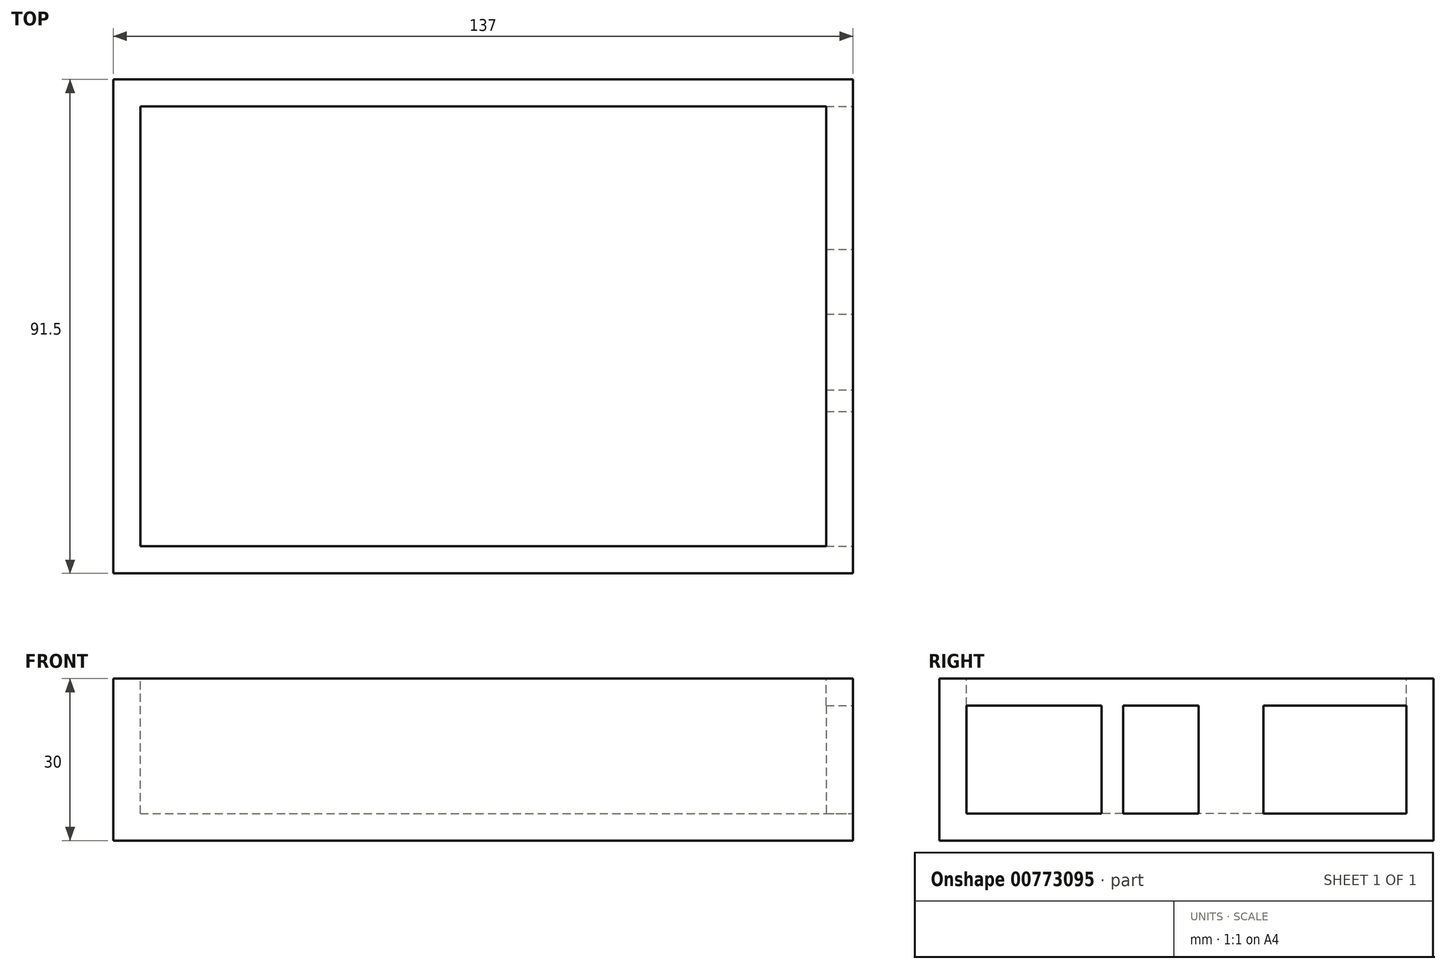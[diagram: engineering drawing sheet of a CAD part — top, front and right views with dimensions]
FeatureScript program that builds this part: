
annotation { "Feature Type Name" : "Feature", "Feature Type Description" : "" }
export const myFeature = defineFeature(function(context is Context, id is Id, definition is map)
    precondition{}
    {
        {
            var Q0;
            Q0=qCreatedBy(makeId("Top.planeOp"),FACE);
            var sketch = newSketch(context, id + "F0", { "sketchPlane" : qUnion([Q0])});
            skLineSegment(sketch, "E0.bottom", {"start": v(-74.24, 56.87) * mm, "end": v(62.76, 56.87) * mm});
            skLineSegment(sketch, "E0.top", {"start": v(-74.24, -34.63) * mm, "end": v(62.76, -34.63) * mm});
            skLineSegment(sketch, "E0.left", {"start": v(-74.24, 56.87) * mm, "end": v(-74.24, -34.63) * mm});
            skLineSegment(sketch, "E0.right", {"start": v(62.76, 56.87) * mm, "end": v(62.76, -34.63) * mm});
            skSolve(sketch);
        }
        {
            var Q0;
            Q0=makeQuery(id+"F0.imprint","IMPRINT",FACE,{"disambiguationData":[TD([[makeQuery(id+"F0.imprint","IMPRINT",EDGE,{"derivedFrom":sQuery(id+"F0.wireOp",EDGE,"E0.bottom")}),-1.0]])]});
            extrude(context, id + "F1", {"entities" : qUnion([Q0]), "depth" : 30 * mm, "offsetDistance" : 25 * mm});
        }
        {
            var Q0;
            Q0=makeQuery(id+"F1.opExtrude","CAP_FACE",FACE,{"disambiguationData":[OSD([sQuery(id+"F0.wireOp",EDGE,"E0.bottom"),sQuery(id+"F0.wireOp",EDGE,"E0.top"),sQuery(id+"F0.wireOp",EDGE,"E0.left"),sQuery(id+"F0.wireOp",EDGE,"E0.right")])],"isStart":false});
            var sketch = newSketch(context, id + "F2", { "sketchPlane" : qUnion([Q0])});
            skLineSegment(sketch, "E1", {"start": v(-74.24, 56.87) * mm, "end": v(-74.24, 51.87) * mm, "construction": true});
            skLineSegment(sketch, "E2", {"start": v(-74.24, 51.87) * mm, "end": v(-69.24, 51.87) * mm, "construction": true});
            skLineSegment(sketch, "E3", {"start": v(62.76, -34.63) * mm, "end": v(57.76, -34.63) * mm, "construction": true});
            skLineSegment(sketch, "E4", {"start": v(57.76, -34.63) * mm, "end": v(57.76, -29.63) * mm, "construction": true});
            skLineSegment(sketch, "E5.bottom", {"start": v(-69.24, 51.87) * mm, "end": v(57.76, 51.87) * mm});
            skLineSegment(sketch, "E5.top", {"start": v(-69.24, -29.63) * mm, "end": v(57.76, -29.63) * mm});
            skLineSegment(sketch, "E5.left", {"start": v(-69.24, 51.87) * mm, "end": v(-69.24, -29.63) * mm});
            skLineSegment(sketch, "E5.right", {"start": v(57.76, 51.87) * mm, "end": v(57.76, -29.63) * mm});
            skSolve(sketch);
        }
        {
            var Q0;
            Q0=makeQuery(id+"F2.imprint","IMPRINT",FACE,{"disambiguationData":[TD([[makeQuery(id+"F2.imprint","IMPRINT",EDGE,{"derivedFrom":sQuery(id+"F2.wireOp",EDGE,"E5.bottom")}),-1.0]])]});
            extrude(context, id + "F3", {"entities" : qUnion([Q0]), "operationType" : NewBodyOperationType.REMOVE, "oppositeDirection" : true, "depth" : 25 * mm, "offsetDistance" : 25 * mm});
        }
        {
            var Q0;
            Q0=makeQuery(id+"F1.opExtrude","SWEPT_FACE",FACE,{"disambiguationData":[OSD([sQuery(id+"F0.wireOp",EDGE,"E0.right")])]});
            var sketch = newSketch(context, id + "F4", { "sketchPlane" : qUnion([Q0])});
            skLineSegment(sketch, "E6", {"start": v(-34.63, 30) * mm, "end": v(-34.63, 25) * mm, "construction": true});
            skLineSegment(sketch, "E7", {"start": v(-34.63, 25) * mm, "end": v(56.87, 25) * mm, "construction": true});
            skLineSegment(sketch, "E8.bottom", {"start": v(-4.63, 25) * mm, "end": v(-0.63, 25) * mm});
            skLineSegment(sketch, "E8.top", {"start": v(-4.63, 5) * mm, "end": v(-0.63, 5) * mm});
            skLineSegment(sketch, "E8.left", {"start": v(-4.63, 25) * mm, "end": v(-4.63, 5) * mm});
            skLineSegment(sketch, "E8.right", {"start": v(-0.63, 25) * mm, "end": v(-0.63, 5) * mm});
            skLineSegment(sketch, "E9", {"start": v(-34.63, 25) * mm, "end": v(-34.63, 5) * mm, "construction": true});
            skLineSegment(sketch, "E10", {"start": v(-34.63, 5) * mm, "end": v(-29.63, 5) * mm, "construction": true});
            skLineSegment(sketch, "E11.bottom", {"start": v(-4.63, 25) * mm, "end": v(-29.63, 25) * mm});
            skLineSegment(sketch, "E11.top", {"start": v(-4.63, 5) * mm, "end": v(-29.63, 5) * mm});
            skLineSegment(sketch, "E11.right", {"start": v(-29.63, 25) * mm, "end": v(-29.63, 5) * mm});
            skLineSegment(sketch, "E12", {"start": v(-0.63, 5) * mm, "end": v(13.37, 5) * mm, "construction": true});
            skLineSegment(sketch, "E13", {"start": v(13.37, 5) * mm, "end": v(25.37, 5) * mm, "construction": true});
            skLineSegment(sketch, "E14.bottom", {"start": v(-0.63, 25) * mm, "end": v(13.37, 25) * mm});
            skLineSegment(sketch, "E14.top", {"start": v(-0.63, 5) * mm, "end": v(13.37, 5) * mm});
            skLineSegment(sketch, "E14.right", {"start": v(13.37, 25) * mm, "end": v(13.37, 5) * mm});
            skLineSegment(sketch, "E15.bottom", {"start": v(13.37, 25) * mm, "end": v(25.37, 25) * mm});
            skLineSegment(sketch, "E15.top", {"start": v(13.37, 5) * mm, "end": v(25.37, 5) * mm});
            skLineSegment(sketch, "E15.right", {"start": v(25.37, 25) * mm, "end": v(25.37, 5) * mm});
            skLineSegment(sketch, "E16", {"start": v(56.87, 25) * mm, "end": v(56.87, 5) * mm, "construction": true});
            skLineSegment(sketch, "E17", {"start": v(56.87, 5) * mm, "end": v(51.87, 5) * mm, "construction": true});
            skLineSegment(sketch, "E18.bottom", {"start": v(25.37, 25) * mm, "end": v(51.87, 25) * mm});
            skLineSegment(sketch, "E18.top", {"start": v(25.37, 5) * mm, "end": v(51.87, 5) * mm});
            skLineSegment(sketch, "E18.right", {"start": v(51.87, 25) * mm, "end": v(51.87, 5) * mm});
            skSolve(sketch);
        }
        {
            var Q0;
            Q0=makeQuery(id+"F4.imprint","IMPRINT",FACE,{"disambiguationData":[TD([[makeQuery(id+"F4.imprint","IMPRINT",EDGE,{"derivedFrom":sQuery(id+"F4.wireOp",EDGE,"E11.bottom")}),1.0]])]});
            var Q1;
            Q1=makeQuery(id+"F4.imprint","IMPRINT",FACE,{"disambiguationData":[TD([[makeQuery(id+"F4.imprint","IMPRINT",EDGE,{"derivedFrom":sQuery(id+"F4.wireOp",EDGE,"E14.bottom")}),-1.0]])]});
            var Q2;
            Q2=makeQuery(id+"F4.imprint","IMPRINT",FACE,{"disambiguationData":[TD([[makeQuery(id+"F4.imprint","IMPRINT",EDGE,{"derivedFrom":sQuery(id+"F4.wireOp",EDGE,"E18.bottom")}),-1.0]])]});
            extrude(context, id + "F5", {"entities" : qUnion([Q0, Q1, Q2]), "operationType" : NewBodyOperationType.REMOVE, "oppositeDirection" : true, "depth" : 5 * mm, "offsetDistance" : 25 * mm});
        }
    });
